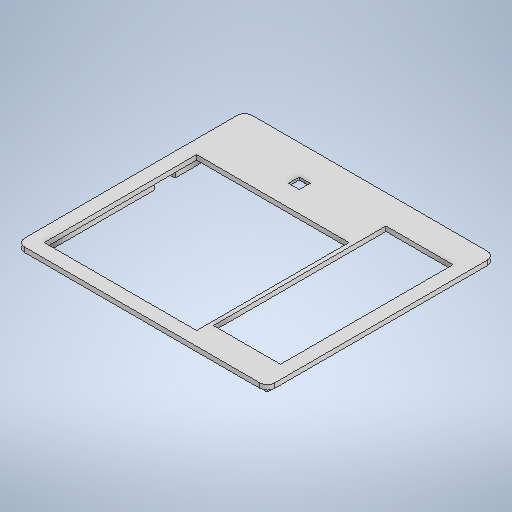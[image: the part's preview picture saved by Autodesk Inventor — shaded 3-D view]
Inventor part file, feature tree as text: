
AUTODESK INVENTOR PART (.ipt)
format: ipt  version: 2025.2 (Build 292293000, 293)  size: 310,784 bytes
history: native  units: in
note: dims shown in document units (in); Inventor stores cm internally (conversion verified against a paired STEP export)
features: extrude x6, sketch x1, fillet x1
ambient origin geometry x8: Origin, YZ Plane, XZ Plane, XY Plane, X Axis, Y Axis, Z Axis, Center Point
bodies: Solid1 (feature_tree)
feature tree (8):
  sketch  "Sketch1"  dims[d0=1.1024in d1=2.8346in d2=0.0079in d3=0.0591in d4=0.1181in d5=0.0in d6=0.0787in d7=0.0in d8=0.0787in d9=0.0in d10=2.5827in d11=2.5827in d12=0.0394in d13=1.0in d14=0.0in d15=0.252in d16=0.252in d17=0.1772in d18=0.1772in d19=0.1181in d20=0.0in d21=0.0394in d22=0.0in d23=0.125in d24=0.0344in d25=0.5in d26=0.0344in]
  extrude  "Extrusion1"  Depth=2.8346in
  extrude  "Extrusion2"  Depth=0.125in
  extrude  "Extrusion3"  Depth=0.0591in
  extrude  "Extrusion4"  Depth=0.1181in TaperAngle=0.0deg
  extrude  "Extrusion5"  Depth=0.0787in TaperAngle=0.0deg
  extrude  "Extrusion6"  Depth=0.0787in TaperAngle=0.0deg
  fillet  "Fillet1"  Radius=2.5827in
